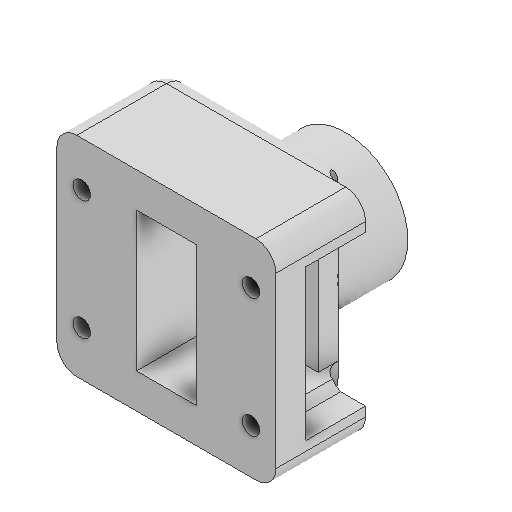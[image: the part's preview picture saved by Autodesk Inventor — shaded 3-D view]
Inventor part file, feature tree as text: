
AUTODESK INVENTOR PART (.ipt)
format: ipt  version: 2022 (Build 260153000, 153)  size: 417,792 bytes
history: native  units: mm
features: extrude x10, sketch x10, fillet x1
ambient origin geometry x8: Origin, YZ Plane, XZ Plane, XY Plane, X Axis, Y Axis, Z Axis, Center Point
bodies: Solid1 (feature_tree)
feature tree (21):
  extrude  "Extrusion1"  Depth=21.0mm
  extrude  "Extrusion2"  Depth=11.0mm
  extrude  "Extrusion3"  Depth=6.0mm
  extrude  "Extrusion4"  Depth=14.0mm
  extrude  "Extrusion5"  Depth=1.75mm
  extrude  "Extrusion6"  Depth=1.75mm
  extrude  "Extrusion7"  Depth=6.0mm
  fillet  "Fillet1"  Radius=6.0mm
  extrude  "Extrusion9"  Depth=8.5mm
  extrude  "Extrusion10"  Depth=6.0mm
  extrude  "Extrusion11"  Depth=2.0mm
  sketch  "Sketch1"  dims[d0=22.0mm d1=21.0mm]
  sketch  "Sketch2"  dims[d2=10.5mm d3=11.0mm]
  sketch  "Sketch3"  dims[d4=4.0mm d5=0.0mm d6=6.0mm]
  sketch  "Sketch4"  dims[d7=3.0mm d8=14.0mm]
  sketch  "Sketch5"  dims[d9=7.0mm d10=1.75mm]
  sketch  "Sketch6"  dims[d11=1.75mm d12=1.75mm]
  sketch  "Sketch7"  dims[d13=1.75mm d14=6.0mm d15=6.0mm]
  sketch  "Sketch9"  dims[d16=8.5mm d17=8.5mm]
  sketch  "Sketch10"  dims[d18=8.5mm d19=6.0mm]
  sketch  "Sketch12"  dims[d20=6.0mm d21=8.5mm d22=4.0mm d23=0.0mm d24=2.7mm d25=2.7mm d26=2.7mm d27=2.7mm d28=1.8mm d29=0.0mm d30=8.0mm d31=3.5mm d32=14.0mm d33=3.5mm d34=6.0mm d35=0.0mm d36=12.5mm d37=2.0mm d38=0.0mm d39=12.5mm d40=7.0mm d41=0.0mm d42=1.0mm d43=0.0mm d46=2.0mm d47=20.0mm d48=0.0mm d49=1.8mm d50=0.0mm d51=4.0mm d52=4.0mm d53=8.0mm d54=0.0mm]
